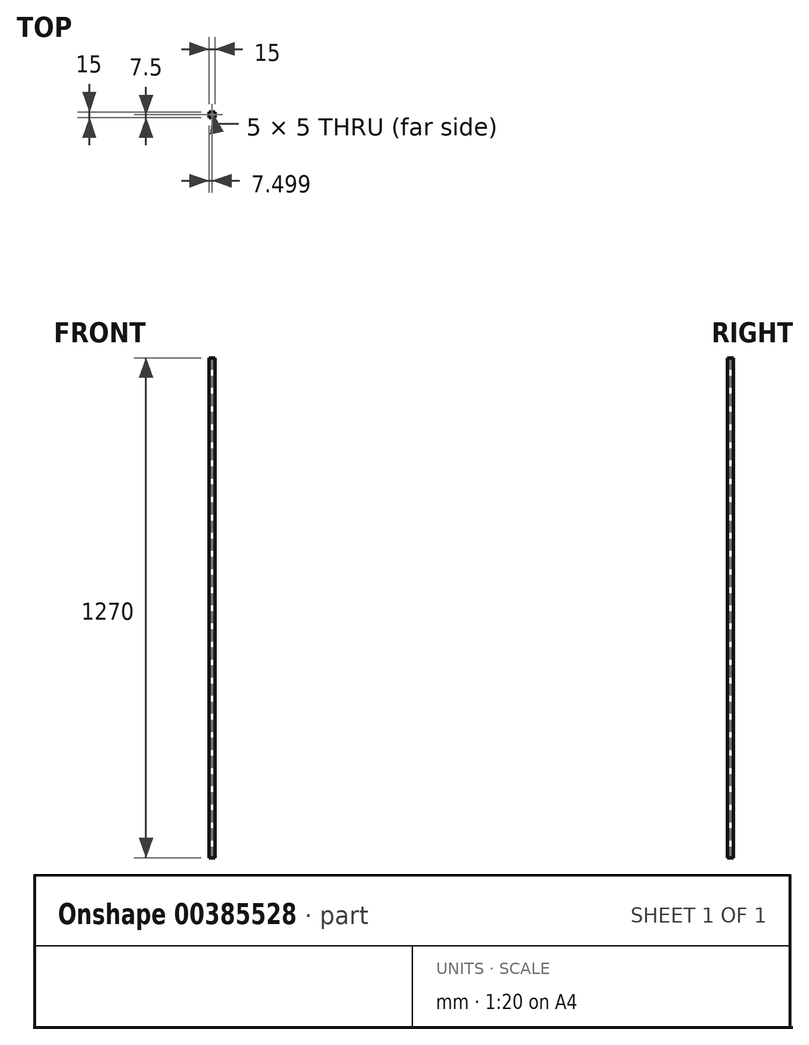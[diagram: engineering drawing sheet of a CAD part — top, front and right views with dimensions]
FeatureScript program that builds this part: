
annotation { "Feature Type Name" : "Feature", "Feature Type Description" : "" }
export const myFeature = defineFeature(function(context is Context, id is Id, definition is map)
    precondition{}
    {
        {
            var Q0;
            Q0=qCreatedBy(makeId("Front.planeOp"),FACE);
            var sketch = newSketch(context, id + "F0", { "sketchPlane" : qUnion([Q0])});
            skLineSegment(sketch, "E0.bottom", {"start": v(-59.1, 1197.9) * mm, "end": v(-44.1, 1197.9) * mm});
            skLineSegment(sketch, "E0.top", {"start": v(-59.1, -72.1) * mm, "end": v(-44.1, -72.1) * mm});
            skLineSegment(sketch, "E0.left", {"start": v(-59.1, 1197.9) * mm, "end": v(-59.1, -72.1) * mm});
            skLineSegment(sketch, "E0.right", {"start": v(-44.1, 1197.9) * mm, "end": v(-44.1, -72.1) * mm});
            skSolve(sketch);
        }
        {
            var Q0;
            Q0=makeQuery(id+"F0.imprint","IMPRINT",FACE,{"disambiguationData":[TD([[makeQuery(id+"F0.imprint","IMPRINT",EDGE,{"derivedFrom":sQuery(id+"F0.wireOp",EDGE,"E0.bottom")}),-1.0]])]});
            extrude(context, id + "F1", {"entities" : qUnion([Q0]), "endBound" : BoundingType.SYMMETRIC, "depth" : 15 * mm});
        }
        {
            var Q0;
            Q0=makeQuery(id+"F1.opExtrude","SWEPT_FACE",FACE,{"disambiguationData":[OSD([sQuery(id+"F0.wireOp",EDGE,"E0.top")])]});
            var sketch = newSketch(context, id + "F2", { "sketchPlane" : qUnion([Q0])});
            skLineSegment(sketch, "E1.0", {"start": v(-54.1, -2.5) * mm, "end": v(-49.1, -2.5) * mm});
            skLineSegment(sketch, "E1.1", {"start": v(-54.1, 2.5) * mm, "end": v(-54.1, -2.5) * mm});
            skLineSegment(sketch, "E1.2", {"start": v(-49.1, 2.5) * mm, "end": v(-54.1, 2.5) * mm});
            skLineSegment(sketch, "E1.3", {"start": v(-49.1, -2.5) * mm, "end": v(-49.1, 2.5) * mm});
            skSolve(sketch);
        }
        {
            var Q0;
            Q0=makeQuery(id+"F2.imprint","IMPRINT",FACE,{"disambiguationData":[TD([[makeQuery(id+"F2.imprint","IMPRINT",EDGE,{"derivedFrom":sQuery(id+"F2.wireOp",EDGE,"E1.0")}),1.0]])]});
            extrude(context, id + "F3", {"entities" : qUnion([Q0]), "operationType" : NewBodyOperationType.REMOVE, "oppositeDirection" : true, "depth" : 1270 * mm});
        }
    });
